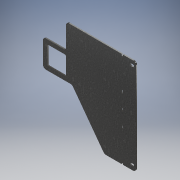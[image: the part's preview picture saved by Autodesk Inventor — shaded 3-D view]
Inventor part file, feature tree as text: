
AUTODESK INVENTOR PART (.ipt)
format: ipt  version: 2017 (Build 210142000, 142)  size: 276,992 bytes
history: native  units: mm
features: fillet x3, extrude x2, sketch x2, other x1
ambient origin geometry x8: Origin, YZ Plane, XZ Plane, XY Plane, X Axis, Y Axis, Z Axis, Center Point
bodies: Body1 (feature_tree)
feature tree (8):
  other  "Sólido1"
  extrude  "Extrusión1"  Depth=101.6mm
  fillet  "Empalme1"  Radius=95.25mm
  fillet  "Empalme2"  Radius=111.125mm
  extrude  "Extrusión2"  Depth=5.0mm TaperAngle=0.0deg
  fillet  "Empalme3"  Radius=12.7mm
  sketch  "Boceto1"  dims[d0=288.925mm d1=101.6mm d2=95.25mm d3=111.125mm]
  sketch  "Boceto2"  dims[d4=393.7mm d7=5.0mm d8=0.0mm d9=12.7mm d10=6.35mm d11=76.2mm d17=17.4625mm d18=19.05mm d19=76.2mm d20=5.55625mm d22=6.35mm d24=53.975mm d42=10.0mm d43=19.05mm d44=15.875mm d45=8.929688mm d46=0.0mm d47=10.0mm d50=130.175mm d51=133.35mm d52=53.975mm d53=5.55625mm d54=6.35mm d67=15.875mm d68=19.05mm d69=5.55625mm d70=5.55625mm d71=5.55625mm d72=13.096875mm d73=13.096875mm d74=13.096875mm d75=53.975mm d80=63.5mm d81=63.5mm d82=127.0mm d83=3.571875mm d87=10.0mm d88=10.0mm d89=17.4625mm d90=10.0mm d91=10.0mm d92=17.4625mm]
